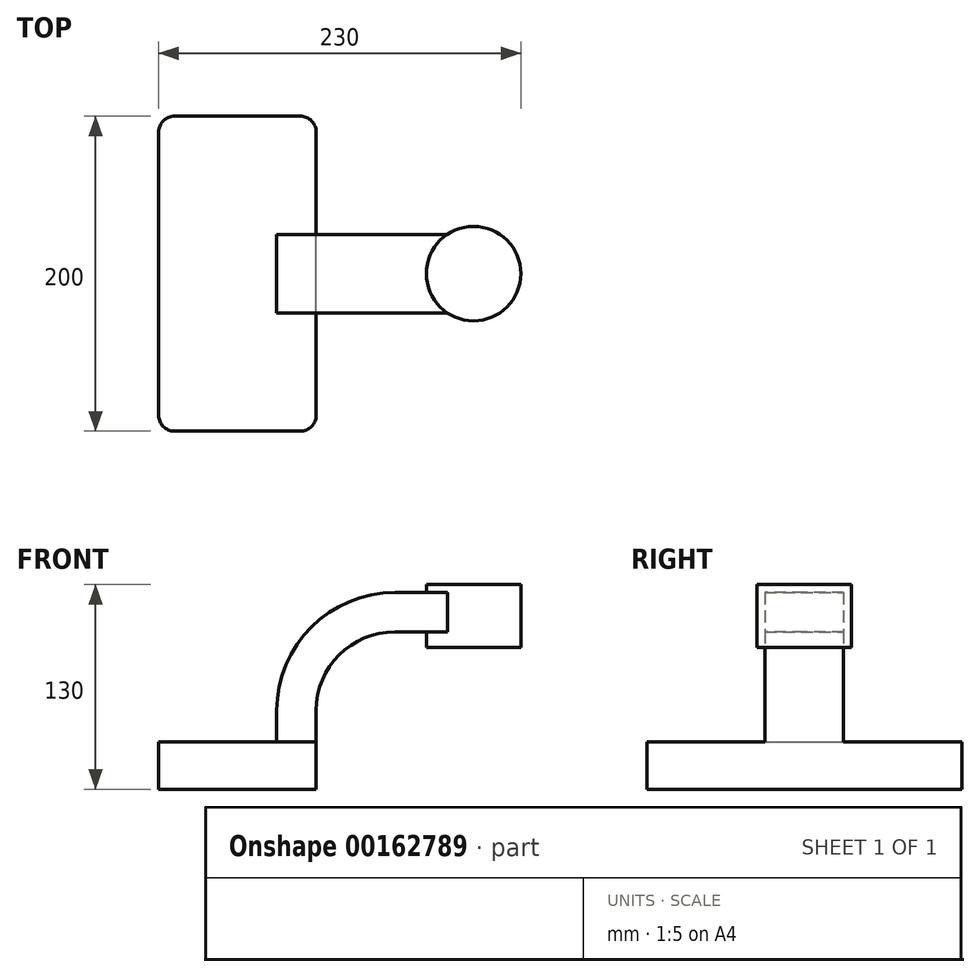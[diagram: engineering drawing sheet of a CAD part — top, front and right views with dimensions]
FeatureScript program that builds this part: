
annotation { "Feature Type Name" : "Feature", "Feature Type Description" : "" }
export const myFeature = defineFeature(function(context is Context, id is Id, definition is map)
    precondition{}
    {
        {
            var Q0;
            Q0=qCreatedBy(makeId("Front.planeOp"),FACE);
            var sketch = newSketch(context, id + "F0", { "sketchPlane" : qUnion([Q0])});
            skLineSegment(sketch, "E0.bottom", {"start": v(-50, -15) * mm, "end": v(50, -15) * mm});
            skLineSegment(sketch, "E0.top", {"start": v(-50, 15) * mm, "end": v(50, 15) * mm});
            skLineSegment(sketch, "E0.left", {"start": v(-50, -15) * mm, "end": v(-50, 15) * mm});
            skLineSegment(sketch, "E0.right", {"start": v(50, -15) * mm, "end": v(50, 15) * mm});
            skPoint(sketch, "E0.middle", {"position": v(0, 0) * mm});
            skLineSegment(sketch, "E1.bottom", {"start": v(120, 75) * mm, "end": v(180, 75) * mm});
            skLineSegment(sketch, "E1.top", {"start": v(120, 115) * mm, "end": v(180, 115) * mm});
            skLineSegment(sketch, "E1.left", {"start": v(120, 75) * mm, "end": v(120, 115) * mm});
            skLineSegment(sketch, "E1.right", {"start": v(180, 75) * mm, "end": v(180, 115) * mm});
            skPoint(sketch, "E1.middle", {"position": v(150, 95) * mm});
            skLineSegment(sketch, "E2", {"start": v(50, 15) * mm, "end": v(50, 35) * mm});
            skArc(sketch, "E3", {"start": v(50, 35) * mm, "mid": v(64.64, 70.36) * mm, "end": v(100, 85) * mm});
            skLineSegment(sketch, "E4", {"start": v(100, 85) * mm, "end": v(150, 85) * mm});
            skLineSegment(sketch, "E5.0", {"start": v(100, 110) * mm, "end": v(150, 110) * mm});
            skArc(sketch, "E5.1", {"start": v(25, 35) * mm, "mid": v(46.97, 88.03) * mm, "end": v(100, 110) * mm});
            skLineSegment(sketch, "E5.2", {"start": v(25, 15) * mm, "end": v(25, 35) * mm});
            skFitSpline(sketch, "E6", {"points": [v(100, 110) * mm, v(-50, 15) * mm], "startDerivative": vector(-195.56, 1.2) * mm, "endDerivative": vector(-48.46, -167.26) * mm});
            skLineSegment(sketch, "E7", {"start": v(150, 75) * mm, "end": v(150, 115) * mm});
            skSolve(sketch);
        }
        {
            var Q0;
            Q0=makeQuery(id+"F0.imprint","IMPRINT",FACE,{"disambiguationData":[TD([[makeQuery(id+"F0.imprint","IMPRINT",EDGE,{"derivedFrom":sQuery(id+"F0.wireOp",EDGE,"E0.bottom")}),1.0]])]});
            extrude(context, id + "F1", {"entities" : qUnion([Q0]), "endBound" : BoundingType.SYMMETRIC, "depth" : 200 * mm});
        }
        {
            var Q0;
            {var subQ1=sQuery(id+"F0.wireOp",EDGE,"E2");Q0=makeQuery(id+"F0.imprint","IMPRINT",FACE,{"disambiguationData":[TD([[makeQuery(id+"F0.imprint","IMPRINT",EDGE,{"derivedFrom":subQ1}),1.0]])]});}
            var Q1;
            {var subQ0=sQuery(id+"F0.wireOp",EDGE,"E4");var subQ1=sQuery(id+"F0.wireOp",EDGE,"E1.left");var subQ2=makeQuery(id+"F0.imprint","INTERSECT",VERTEX,{"derivedFrom":[subQ1,subQ0]});Q1=makeQuery(id+"F0.imprint","IMPRINT",FACE,{"disambiguationData":[TD([[makeQuery(id+"F0.imprint","IMPRINT",EDGE,{"disambiguationData":[TD([[subQ2,-1.0]])],"derivedFrom":subQ1}),-1.0]])]});}
            extrude(context, id + "F2", {"entities" : qUnion([Q0, Q1]), "operationType" : NewBodyOperationType.ADD, "endBound" : BoundingType.SYMMETRIC, "depth" : 50 * mm});
        }
        {
            var Q0;
            Q0=makeQuery(id+"F0.imprint","IMPRINT",FACE,{"disambiguationData":[TD([[makeQuery(id+"F0.imprint","IMPRINT",EDGE,{"derivedFrom":sQuery(id+"F0.wireOp",EDGE,"E5.1")}),1.0]])]});
            extrude(context, id + "F3", {"entities" : qUnion([Q0]), "operationType" : NewBodyOperationType.ADD, "endBound" : BoundingType.SYMMETRIC, "depth" : 20 * mm});
        }
        {
            var Q0;
            {var subQ0=sQuery(id+"F0.wireOp",EDGE,"E1.right");Q0=makeQuery(id+"F0.imprint","IMPRINT",FACE,{"disambiguationData":[TD([[makeQuery(id+"F0.imprint","IMPRINT",EDGE,{"derivedFrom":subQ0}),1.0]])]});}
            var Q1;
            Q1=sQuery(id+"F0.wireOp",EDGE,"E7");
            revolve(context, id + "F4", {"operationType" : NewBodyOperationType.ADD, "entities" : qUnion([Q0]), "axis" : qUnion([Q1]), "revolveType" : RevolveType.FULL});
        }
        {
            var Q0;
            Q0=makeQuery(id+"F1.opExtrude","CAP_EDGE",EDGE,{"disambiguationData":[OSD([sQuery(id+"F0.wireOp",EDGE,"E0.right")])],"isStart":false});
            var Q1;
            Q1=makeQuery(id+"F1.opExtrude","CAP_EDGE",EDGE,{"disambiguationData":[OSD([sQuery(id+"F0.wireOp",EDGE,"E0.left")])],"isStart":false});
            var Q2;
            Q2=makeQuery(id+"F1.opExtrude","CAP_EDGE",EDGE,{"disambiguationData":[OSD([sQuery(id+"F0.wireOp",EDGE,"E0.right")])],"isStart":true});
            var Q3;
            Q3=makeQuery(id+"F1.opExtrude","CAP_EDGE",EDGE,{"disambiguationData":[OSD([sQuery(id+"F0.wireOp",EDGE,"E0.left")])],"isStart":true});
            fillet(context, id + "F5", {"entities" : qUnion([Q0, Q1, Q2, Q3]), "radius" : 10 * mm, "tangentPropagation" : true, "allowEdgeOverflow" : false});
        }
    });
